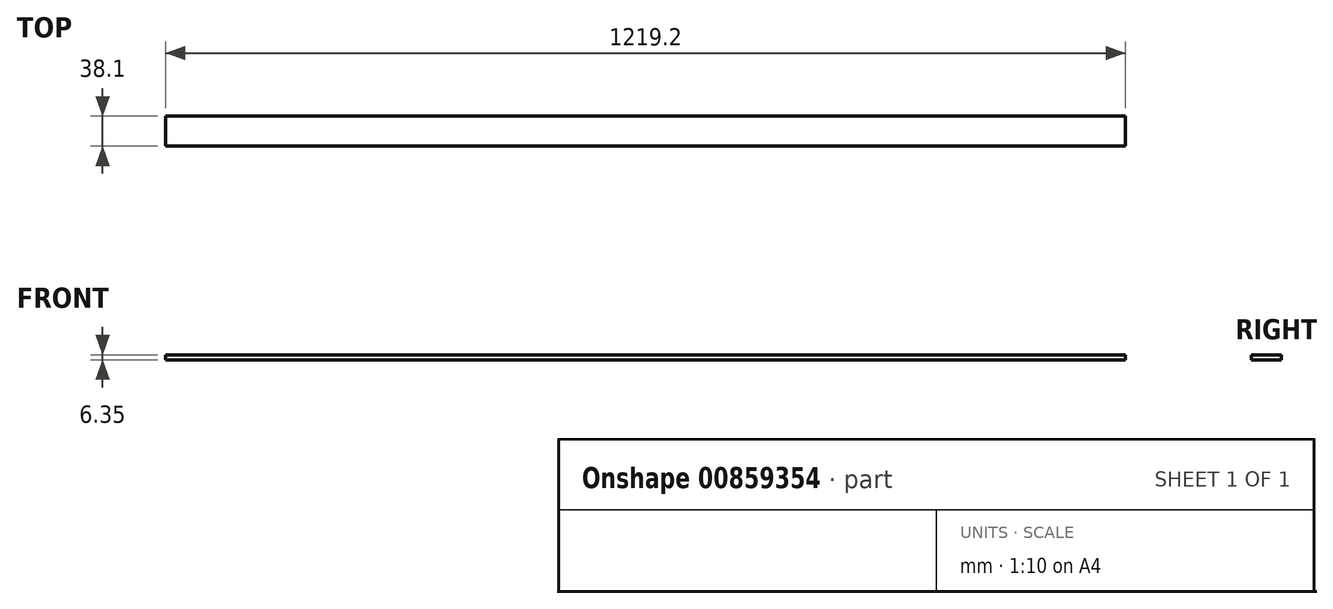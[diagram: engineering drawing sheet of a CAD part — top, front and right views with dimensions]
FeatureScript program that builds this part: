
annotation { "Feature Type Name" : "Feature", "Feature Type Description" : "" }
export const myFeature = defineFeature(function(context is Context, id is Id, definition is map)
    precondition{}
    {
        {
            var Q0;
            Q0=qCreatedBy(makeId("Top.planeOp"),FACE);
            var sketch = newSketch(context, id + "F0", { "sketchPlane" : qUnion([Q0])});
            skLineSegment(sketch, "E0.bottom", {"start": v(-1136.88, 42.6) * mm, "end": v(82.32, 42.6) * mm});
            skLineSegment(sketch, "E0.top", {"start": v(-1136.88, 4.5) * mm, "end": v(82.32, 4.5) * mm});
            skLineSegment(sketch, "E0.left", {"start": v(-1136.88, 42.6) * mm, "end": v(-1136.88, 4.5) * mm});
            skLineSegment(sketch, "E0.right", {"start": v(82.32, 42.6) * mm, "end": v(82.32, 4.5) * mm});
            skSolve(sketch);
        }
        {
            var Q0;
            Q0=makeQuery(id+"F0.imprint","IMPRINT",FACE,{"disambiguationData":[TD([[makeQuery(id+"F0.imprint","IMPRINT",EDGE,{"derivedFrom":sQuery(id+"F0.wireOp",EDGE,"E0.bottom")}),-1.0]])]});
            extrude(context, id + "F1", {"entities" : qUnion([Q0]), "depth" : 6.35 * mm, "offsetDistance" : 25.4 * mm});
        }
    });
